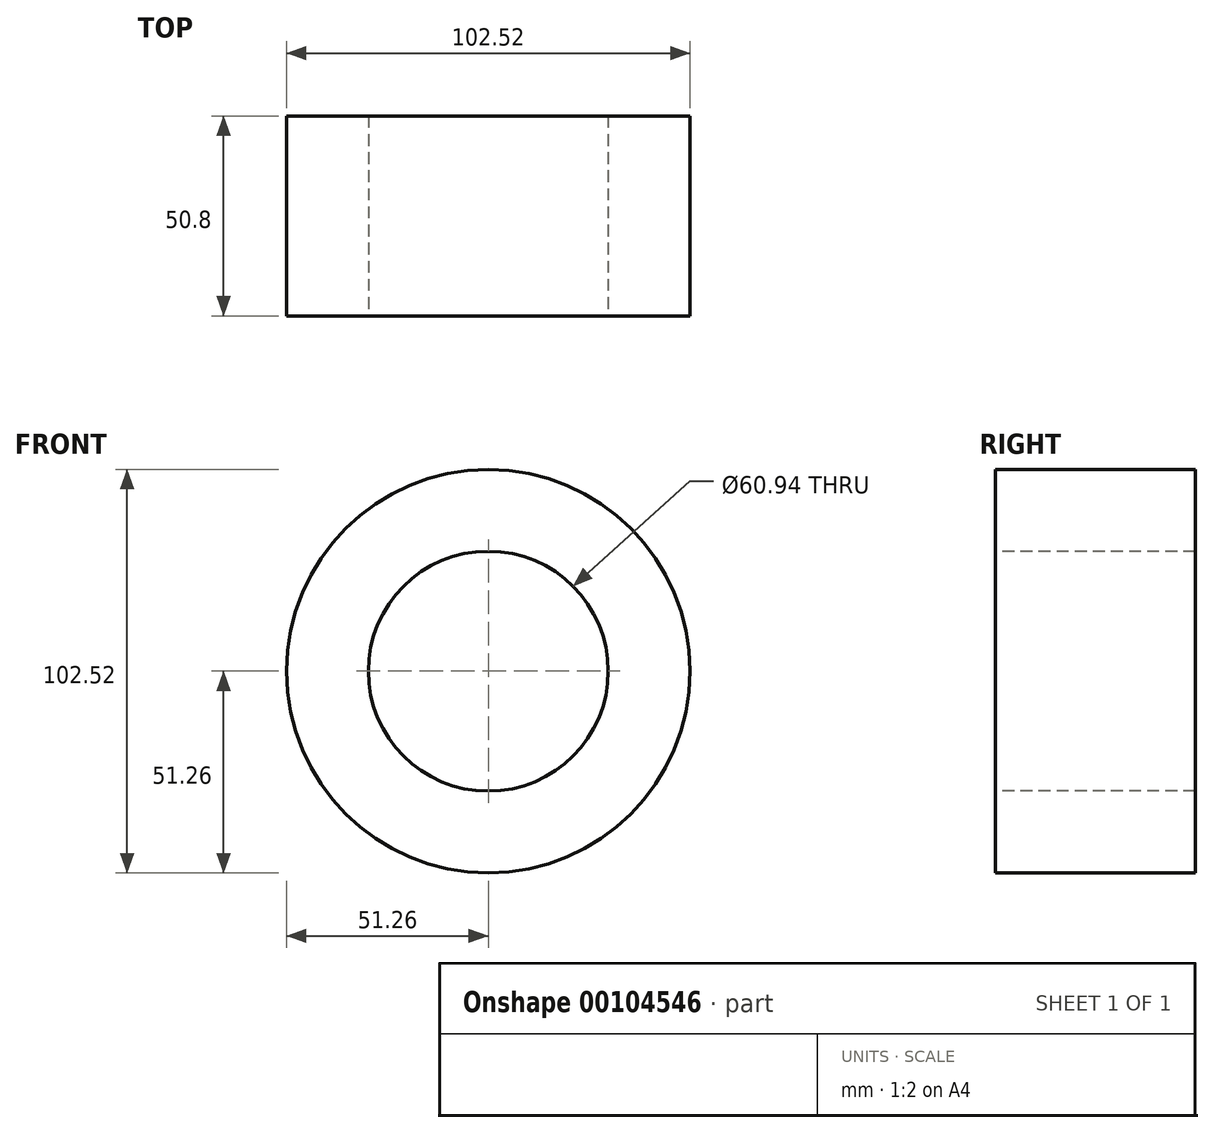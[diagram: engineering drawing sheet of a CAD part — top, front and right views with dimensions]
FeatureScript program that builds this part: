
annotation { "Feature Type Name" : "Feature", "Feature Type Description" : "" }
export const myFeature = defineFeature(function(context is Context, id is Id, definition is map)
    precondition{}
    {
        {
            var Q0;
            Q0=qCreatedBy(makeId("Front.planeOp"),FACE);
            var sketch = newSketch(context, id + "F0", { "sketchPlane" : qUnion([Q0])});
            skCircle(sketch, "E0", {"center": v(0, 0) * mm, "radius": 51.26 * mm});
            skSolve(sketch);
        }
        {
            var Q0;
            Q0=makeQuery(id+"F0.imprint","IMPRINT",FACE,{"disambiguationData":[TD([[makeQuery(id+"F0.imprint","IMPRINT",EDGE,{"derivedFrom":sQuery(id+"F0.wireOp",EDGE,"E0")}),1.0]])]});
            extrude(context, id + "F1", {"entities" : qUnion([Q0]), "depth" : 50.8 * mm});
        }
        {
            var Q0;
            Q0=makeQuery(id+"F1.opExtrude","CAP_FACE",FACE,{"disambiguationData":[OSD([sQuery(id+"F0.wireOp",EDGE,"E0")])],"isStart":false});
            var sketch = newSketch(context, id + "F2", { "sketchPlane" : qUnion([Q0])});
            skCircle(sketch, "E1", {"center": v(0, 0) * mm, "radius": 30.47 * mm});
            skSolve(sketch);
        }
        {
            var Q0;
            Q0 = qSketchRegion(id + "F2", true);
            extrude(context, id + "F3", {"entities" : qUnion([Q0]), "operationType" : NewBodyOperationType.REMOVE, "oppositeDirection" : true, "depth" : 50.8 * mm});
        }
    });
